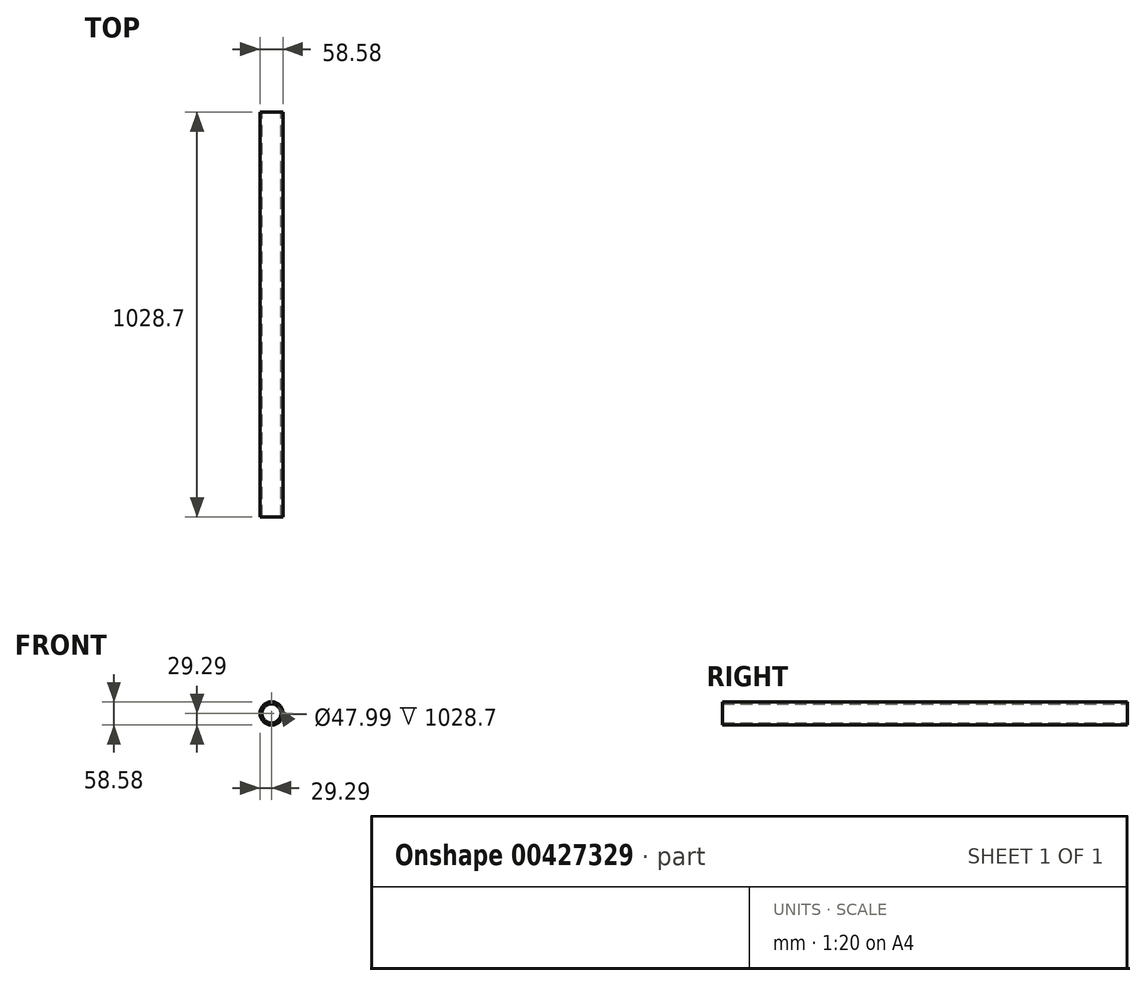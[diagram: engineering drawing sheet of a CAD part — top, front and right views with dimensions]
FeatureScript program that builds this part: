
annotation { "Feature Type Name" : "Feature", "Feature Type Description" : "" }
export const myFeature = defineFeature(function(context is Context, id is Id, definition is map)
    precondition{}
    {
        {
            var Q0;
            Q0=qCreatedBy(makeId("Front.planeOp"),FACE);
            var sketch = newSketch(context, id + "F0", { "sketchPlane" : qUnion([Q0])});
            skCircle(sketch, "E0", {"center": v(0, 0) * mm, "radius": 24 * mm});
            skCircle(sketch, "E1", {"center": v(0, 0) * mm, "radius": 29.3 * mm});
            skSolve(sketch);
        }
        {
            var Q0;
            Q0 = qSketchRegion(id + "F0", true);
            extrude(context, id + "F1", {"entities" : qUnion([Q0]), "depth" : 1028.7 * mm});
        }
    });
